# Revit family: QF_BOURGEAT_NOMAD_Modèle_pour_liaison_chaude
name_source: partatom
category: Equipement spécialisé
revit_build: Autodesk Revit 2015 (Build: 20140606_1530(x64)
units: mm (PartAtom-declared; Revit-internal decimal feet)

## types (12) — shared parameters
Fabricant = BOURGEAT
Fréquence = 50 Hz
Hauteur de porte bas = 409 mm
Hauteur de serrure bas = 172 mm  [stored 0.564304 ft]
Indice de protection = 21
Inox = Acier inoxydable, poli
Phase = 2
Spécification du Fabricant = Modèle pour liaison chaude
Tension = 230 V
URL catalogue = http://www.bourgeat.fr
Vitrage = Verre

## per-type parameters (varying)
| type | 2x4 | 2x8 | Capacité en bacs GN H.65 mm | Charge max | Consommation énergétique | Decalage porte | Hauteur boitier de commande | Hauteur de porte haut | Hauteur de serrure haut | Hauteur hors tout | Hauteur plateau | Intensité nominale | Longueur Pare haleine | Longueur hors tout | Modèle | Nombre de repas | Pare-haleine | Plaque Vitro 1 | Plaque vitro 2 | Poids net à vide | Profondeur hors tout | Puissance électrique  | Rampe |
| 2x4 avec pare-haleine - Dessus inox - neutre | Oui | Non | 2 x 4 GN1/1 | 60.00 kg | 0.42KWh/h | 11 mm  [stored 0.0360892 ft] | 128 mm  [stored 0.419948 ft] | 382 mm | 160 mm  [stored 0.524934 ft] | 1462 mm  [stored 4.79659 ft] | 1062 mm  [stored 3.48425 ft] | 4 A | 897 mm  [stored 2.94291 ft] | 959 mm  [stored 3.14633 ft] | 885230 | jusqu'à 60/80 | Oui | Non | Non | 120.00 kg | 795 mm  [stored 2.60827 ft] | 900 W | Non |
| 2x4 avec pare-haleine - Dessus inox - neutre + lampe(s) | Oui | Non | 2 x 4 GN1/1 | 60.00 kg | 0.42KWh/h | 11 mm  [stored 0.0360892 ft] | 128 mm  [stored 0.419948 ft] | 382 mm | 160 mm  [stored 0.524934 ft] | 1462 mm  [stored 4.79659 ft] | 1062 mm  [stored 3.48425 ft] | 6 A | 897 mm  [stored 2.94291 ft] | 959 mm  [stored 3.14633 ft] | 885234 | jusqu'à 60/80 | Oui | Non | Non | 120.00 kg | 795 mm  [stored 2.60827 ft] | 1400 W | Non |
| 2x4 avec pare-haleine - Dessus 1 plaque vitro + 1 lampe | Oui | Non | 2 x 4 GN1/1 | 60.00 kg | 0.42KWh/h | 11 mm  [stored 0.0360892 ft] | 128 mm  [stored 0.419948 ft] | 382 mm | 160 mm  [stored 0.524934 ft] | 1462 mm  [stored 4.79659 ft] | 1062 mm  [stored 3.48425 ft] | 7 A | 897 mm  [stored 2.94291 ft] | 959 mm  [stored 3.14633 ft] | 885231 | jusqu'à 60/80 | Oui | Oui | Non | 120.00 kg | 795 mm  [stored 2.60827 ft] | 1700 W | Non |
| 2x4 - Dessus inox - neutre | Oui | Non | 2 x 4 GN1/1 | 60.00 kg | 0.42KWh/h | 11 mm  [stored 0.0360892 ft] | 128 mm  [stored 0.419948 ft] | 382 mm | 160 mm  [stored 0.524934 ft] | 1174 mm  [stored 3.85171 ft] | 1062 mm  [stored 3.48425 ft] | 4 A | 897 mm  [stored 2.94291 ft] | 959 mm  [stored 3.14633 ft] | 885330 | jusqu'à 60/80 | Non | Non | Non | 110.00 kg | 791 mm | 900 W | Oui |
| 2x4 - Dessus 1 plaque vitro + 1 lampe | Oui | Non | 2 x 4 GN1/1 | 60.00 kg | 0.42KWh/h | 11 mm  [stored 0.0360892 ft] | 128 mm  [stored 0.419948 ft] | 382 mm | 160 mm  [stored 0.524934 ft] | 1174 mm  [stored 3.85171 ft] | 1062 mm  [stored 3.48425 ft] | 5 A | 897 mm  [stored 2.94291 ft] | 959 mm  [stored 3.14633 ft] | 885331 | jusqu'à 60/80 | Non | Oui | Non | 110.00 kg | 791 mm | 1200 W | Oui |
| 2x8 avec pare-haleine - Dessus inox - neutre | Non | Oui | 2 x 8 GN1/1 | 120.00 kg | 0.54KWh/h | 7 mm  [stored 0.0229659 ft] | 35 mm  [stored 0.114829 ft] | 715 mm  [stored 2.3458 ft] | 306 mm  [stored 1.00394 ft] | 1371 mm  [stored 4.49803 ft] | 968 mm  [stored 3.17585 ft] | 8 A | 1265 mm  [stored 4.15026 ft] | 1327 mm  [stored 4.35367 ft] | 885280 | jusqu'à 100/120 | Oui | Non | Non | 160.00 kg | 795 mm  [stored 2.60827 ft] | 1900 W | Non |
| 2x8 avec pare-haleine - Dessus inox - neutre + lampe(s) | Non | Oui | 2 x 8 GN1/1 | 160.00 kg | 0.54KWh/h | 7 mm  [stored 0.0229659 ft] | 35 mm  [stored 0.114829 ft] | 715 mm  [stored 2.3458 ft] | 306 mm  [stored 1.00394 ft] | 1371 mm  [stored 4.49803 ft] | 968 mm  [stored 3.17585 ft] | 12 A | 1265 mm  [stored 4.15026 ft] | 1327 mm  [stored 4.35367 ft] | 885284 | jusqu'à 100/120 | Oui | Non | Non | 120.00 kg | 795 mm  [stored 2.60827 ft] | 2900 W | Non |
| 2x8 avec pare-haleine - Dessus 1 plaque vitro + 1 lampe | Non | Oui | 2 x 8 GN1/1 | 120.00 kg | 0.54KWh/h | 7 mm  [stored 0.0229659 ft] | 35 mm  [stored 0.114829 ft] | 715 mm  [stored 2.3458 ft] | 306 mm  [stored 1.00394 ft] | 1371 mm  [stored 4.49803 ft] | 968 mm  [stored 3.17585 ft] | 12 A | 1265 mm  [stored 4.15026 ft] | 1327 mm  [stored 4.35367 ft] | 885281 | jusqu'à 100/120 | Oui | Oui | Non | 160.00 kg | 795 mm  [stored 2.60827 ft] | 2700 W | Non |
| 2x8 avec pare-haleine - Dessus 2 plaques vitro + 2 lampes | Non | Oui | 2 x 8 GN1/1 | 120.00 kg | 0.54KWh/h | 7 mm  [stored 0.0229659 ft] | 35 mm  [stored 0.114829 ft] | 715 mm  [stored 2.3458 ft] | 306 mm  [stored 1.00394 ft] | 1371 mm  [stored 4.49803 ft] | 968 mm  [stored 3.17585 ft] | 15 A | 1265 mm  [stored 4.15026 ft] | 1327 mm  [stored 4.35367 ft] | 885282 | jusqu'à 100/120 | Oui | Oui | Oui | 160.00 kg | 795 mm  [stored 2.60827 ft] | 3500 W | Non |
| 2x8 - Dessus inox - neutre | Non | Oui | 2 x 8 GN1/1 | 120.00 kg | 0.54KWh/h | 7 mm  [stored 0.0229659 ft] | 35 mm  [stored 0.114829 ft] | 715 mm  [stored 2.3458 ft] | 306 mm  [stored 1.00394 ft] | 1084 mm  [stored 3.55643 ft] | 968 mm  [stored 3.17585 ft] | 8 A | 1265 mm  [stored 4.15026 ft] | 1327 mm  [stored 4.35367 ft] | 885380 | jusqu'à 100/120 | Non | Non | Non | 140.00 kg | 795 mm  [stored 2.60827 ft] | 1900 W | Oui |
| 2x8 - Dessus 1 plaque vitro + 1 lampe | Non | Oui | 2 x 8 GN1/1 | 120.00 kg | 0.54KWh/h | 7 mm  [stored 0.0229659 ft] | 35 mm  [stored 0.114829 ft] | 715 mm  [stored 2.3458 ft] | 306 mm  [stored 1.00394 ft] | 1084 mm  [stored 3.55643 ft] | 968 mm  [stored 3.17585 ft] | 10 A | 1265 mm  [stored 4.15026 ft] | 1327 mm  [stored 4.35367 ft] | 885381 | jusqu'à 100/120 | Non | Oui | Non | 140.00 kg | 795 mm  [stored 2.60827 ft] | 2200 W | Oui |
| 2x8 - Dessus 2 plaques vitro + 2 lampes | Non | Oui | 2 x 8 GN1/1 | 120.00 kg | 0.54KWh/h | 7 mm  [stored 0.0229659 ft] | 35 mm  [stored 0.114829 ft] | 715 mm  [stored 2.3458 ft] | 306 mm  [stored 1.00394 ft] | 1084 mm  [stored 3.55643 ft] | 968 mm  [stored 3.17585 ft] | 11 A | 1265 mm  [stored 4.15026 ft] | 1327 mm  [stored 4.35367 ft] | 885382 | jusqu'à 100/120 | Non | Oui | Oui | 140.00 kg | 795 mm  [stored 2.60827 ft] | 2500 W | Oui |

note: [stored X ft] marks values corroborated as IEEE doubles in the binary element streams (Revit-internal decimal feet)

## geometry (parser evidence)
native form markers: Blend x2
no freeform markers — native parametric forms only
